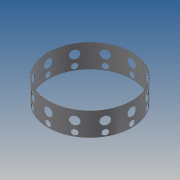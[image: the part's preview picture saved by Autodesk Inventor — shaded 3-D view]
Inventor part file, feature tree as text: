
AUTODESK INVENTOR PART (.ipt)
format: ipt  version: 2014 SP1 (Build 180222100, 222)  size: 305,664 bytes
history: native  units: in
note: dims shown in document units (in); Inventor stores cm internally (conversion verified against a paired STEP export)
features: sketch x5, plane x2, hole x2, pattern_circular x2, extrude x1
ambient origin geometry x8: Origin, YZ Plane, XZ Plane, XY Plane, X Axis, Y Axis, Z Axis, Center Point
bodies: Solid1 (feature_tree)
feature tree (12):
  extrude  "tube"  Depth=0.0394in
  sketch  "Sketch2"  dims[d3=10.0in d4=0.0in d5=1.0in d7=5.9055in]
  plane  "Work Plane1"
  hole  "spar"  [1 undecoded]
  pattern_circular  "spar pattern"  Count=15  [1 undecoded]
  sketch  "Sketch4"  dims[d18=0.0773in]
  plane  "Work Plane2"
  hole  "support"  [1 undecoded]
  pattern_circular  "support pattern"  Count=4  [1 undecoded]
  sketch  "Sketch1"  dims[d0=36.0in d2=0.0394in]
  sketch  "Sketch3"  dims[d8=3.5827in d9=0.75in d10=0.375in d11=0.25in d12=0.5635in d13=1.0in d14=0.8108in d15=4.7244in d16=360.0deg]
  sketch  "Sketch7"  dims[d32=2.5197in d33=1.5748in d34=2.375in d35=0.75in d36=0.375in d37=0.25in d38=0.5635in d39=1.0in d40=0.8108in d41=4.7244in d42=360.0deg d67=4.0945in]
note: 4 required parameter values undecoded (feature->parameter linkage not recoverable at this tier; creation-order binding heuristic only, values carry confidence <= 0.55)
